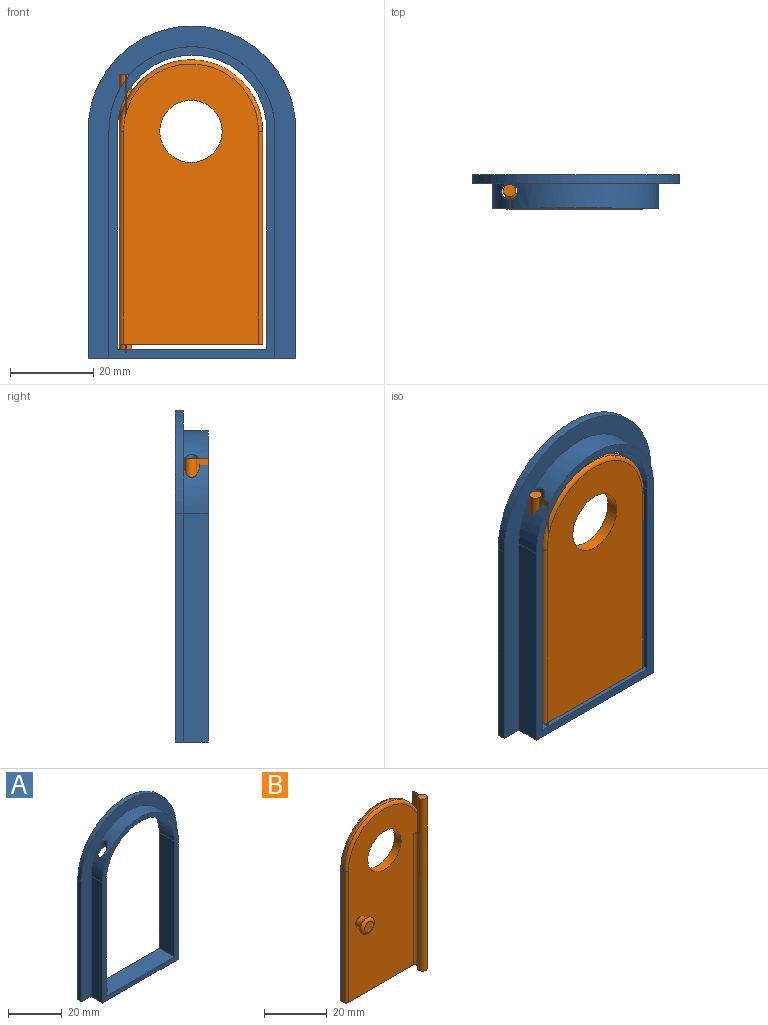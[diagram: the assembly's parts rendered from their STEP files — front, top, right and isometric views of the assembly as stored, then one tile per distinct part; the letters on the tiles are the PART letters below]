
ASSEMBLY  parts=2 mates=1
PART A: 16 faces, bbox 50x8x80 mm
  f0: plane 36x8mm, normal (0,0,1), area 275.4mm2, adj f1,f7,f9,f13,f15
  f1: plane 52.9x8mm, normal (1,0,0), area 423.2mm2, adj f0,f2,f9,f13
  f2: cylinder r=18mm len=36mm, axis (0,1,0), area 419.5mm2, adj f1,f7,f9,f13,f14
  f3: cylinder r=25mm len=50mm, axis (0,1,0), area 157.1mm2, adj f4,f6,f8,f9
  f4: plane 55x2mm, normal (-1,0,0), area 110mm2, adj f3,f5,f8,f9
  f5: plane 50x8mm, normal (0,0,-1), area 327.4mm2, adj f4,f6,f8,f9,f10,f12,f13,f15
  f6: plane 55x2mm, normal (1,0,0), area 110mm2, adj f3,f5,f8,f9
  f7: plane 52.9x8mm, normal (-1,0,0), area 423.2mm2, adj f0,f2,f9,f13
  f8: plane 80x50mm, normal (0,-1,0), area 903.4mm2, adj f3,f4,f5,f6,f10,f11,f12
  f9: plane 80x50mm, normal (0,1,0), area 1318.3mm2, adj f0,f1,f2,f3,f4,f5,f6,f7
  f10: plane 55x6mm, normal (1,0,0), area 330mm2, adj f5,f8,f11,f13
  f11: cylinder r=20mm len=40mm, axis (0,1,0), area 355.6mm2, adj f8,f10,f12,f13,f14
  f12: plane 55x6mm, normal (-1,0,0), area 330mm2, adj f5,f8,f11,f13
  f13: plane 75x40mm, normal (0,-1,0), area 414.9mm2, adj f0,f1,f2,f5,f7,f10,f11,f12
  f14: cylinder r=2mm len=14.28mm, axis (0,0,-1), area 55.4mm2, adj f2,f11
  f15: cylinder r=2mm len=4mm, axis (0,0,-1), area 26.4mm2, adj f0,f5
PART B: 30 faces, bbox 37.3x7.6x71.9 mm
  f0: cylinder r=17.25mm len=32.9mm, axis (0,1,0), area 46.7mm2, adj f3,f4,f7,f27
  f1: plane 32.9x4.4mm, normal (0,0,-1), area 98.8mm2, adj f2,f6,f7,f11,f17,f21,f22,f25
  f2: cylinder r=1.5mm len=67mm, axis (0,0,1), area 474.9mm2, adj f1,f4,f6,f8,f15,f16,f17,f18
  f3: torus R=16.25mm, axis (0,-1,0), area 73.2mm2, adj f0,f11,f21,f27
  f4: torus R=16.25mm, axis (0,-1,0), area 72.8mm2, adj f0,f2,f6,f22,f27
  f5: cylinder r=17.25mm len=6.81mm, axis (0,1,0), area 7mm2, adj f10,f20,f23,f26
  f6: plane 67.5x31.46mm, normal (0,-1,0), area 1733.4mm2, adj f1,f2,f4,f9,f13,f18,f22,f25
  f7: plane 51.25x1mm, normal (-1,0,0), area 51.2mm2, adj f0,f1,f21,f22
  f8: plane 3x1.4mm, normal (0,0,-1), area 3.7mm2, adj f2,f10,f11,f19,f24,f29
  f9: cylinder r=7.5mm len=15mm, axis (0,1,0), area 141.4mm2, adj f6,f11
  f10: plane 51.25x1mm, normal (1,0,0), area 51.2mm2, adj f5,f8,f19,f24
  f11: plane 69.5x32.5mm, normal (0,1,0), area 1906.1mm2, adj f1,f3,f8,f9,f15,f16,f19,f20
  f12: plane 4x4mm, normal (0,-1,0), area 12.6mm2, adj f14
  f13: torus R=7mm, axis (0,-1,0), area 47.3mm2, adj f6,f14
  f14: torus R=2mm, axis (0,-1,0), area 26mm2, adj f12,f13
  f15: plane 5.9x3mm, normal (0,0,-1), area 7.6mm2, adj f2,f11,f28,f29
  f16: plane 5.9x3mm, normal (0,0,1), area 7.6mm2, adj f2,f11,f26,f27
  f17: plane 51.25x0.4mm, normal (-1,0,0), area 20.5mm2, adj f1,f2,f18,f25
  f18: plane 1.96x1.4mm, normal (0,0,1), area 0.6mm2, adj f2,f6,f17,f25
  f19: cylinder r=1mm len=51.25mm, axis (0,0,1), area 80.5mm2, adj f8,f10,f11,f20
  f20: torus R=16.25mm, axis (0,-1,0), area 9.2mm2, adj f5,f11,f19,f26
  f21: cylinder r=1mm len=51.25mm, axis (0,0,-1), area 80.5mm2, adj f1,f3,f7,f11
  f22: cylinder r=1mm len=51.25mm, axis (0,0,1), area 80.5mm2, adj f1,f4,f6,f7
  f23: torus R=16.25mm, axis (0,-1,0), area 8.3mm2, adj f2,f5,f24,f26
  f24: cylinder r=1mm len=51.25mm, axis (0,0,1), area 78.6mm2, adj f2,f8,f10,f23
  f25: cylinder r=1mm len=51.25mm, axis (0,0,1), area 80.5mm2, adj f1,f6,f17,f18
  f26: plane 10.17x2.91mm, normal (1,0,0), area 21.1mm2, adj f2,f5,f11,f16,f20,f23
  f27: plane 9.38x2.91mm, normal (-1,0,0), area 19.8mm2, adj f0,f2,f3,f4,f11,f16
  f28: plane 2.9x2mm, normal (-1,0,0), area 5.8mm2, adj f1,f2,f11,f15
  f29: plane 2.9x2mm, normal (1,0,0), area 5.8mm2, adj f2,f8,f11,f15
PLACE A t=(-40.67,7.16,3.71)mm
PLACE B rot(axis=(0,0,-1),179.9deg) t=(-90.66,-1.03,18.7)mm
MATE cylindrical B.f15 <-> A.f14  axis (0,0,-1) through (-81.67,3.16,5.07)mm
